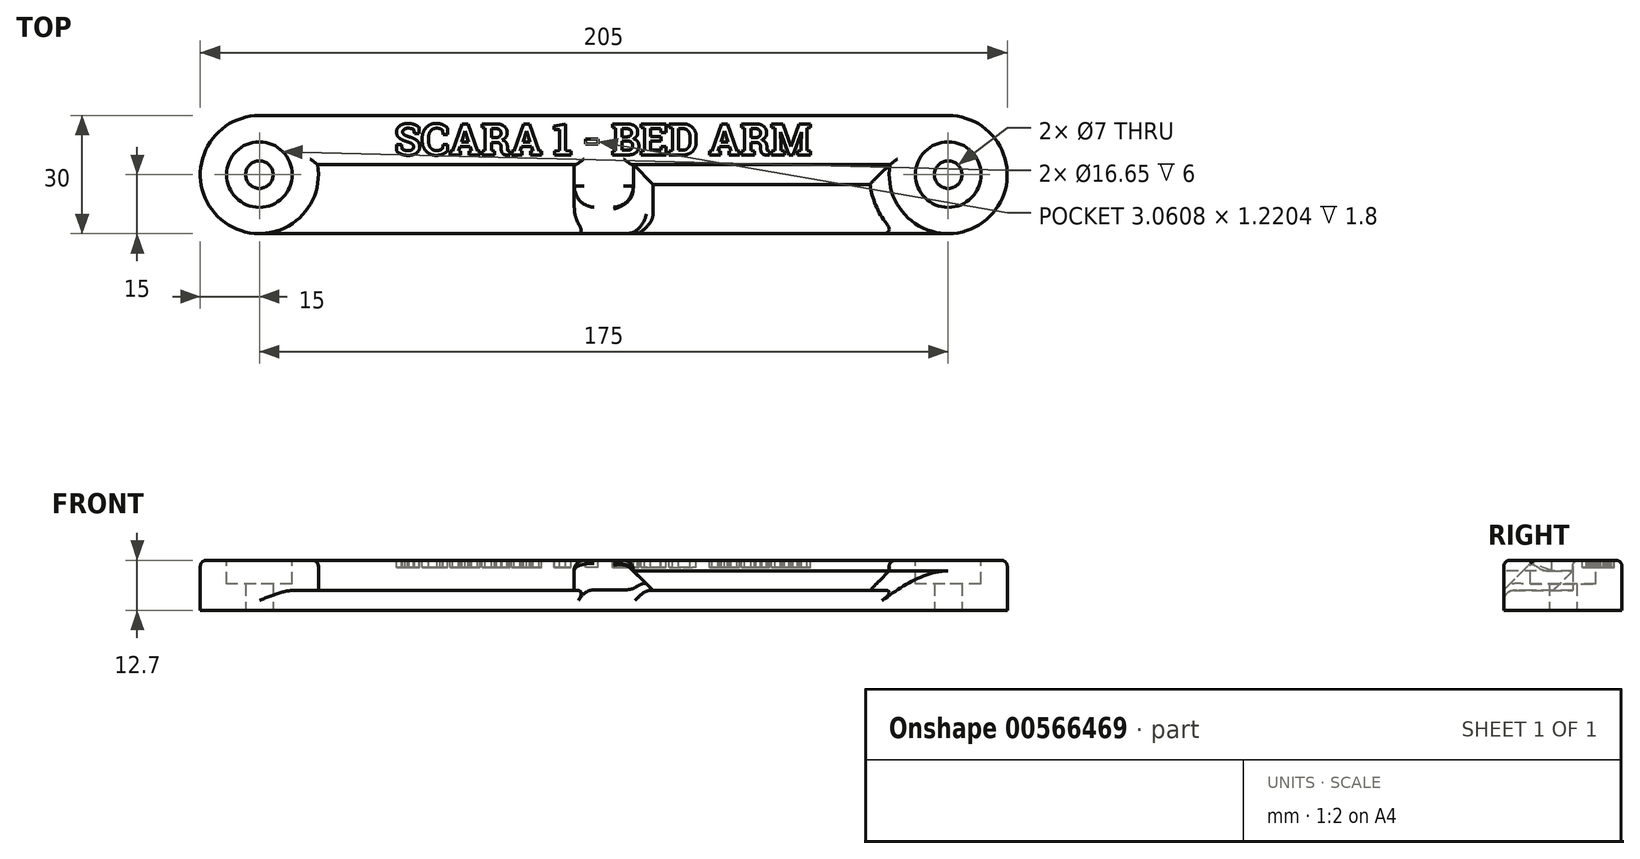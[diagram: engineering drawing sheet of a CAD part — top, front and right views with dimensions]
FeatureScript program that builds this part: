
annotation { "Feature Type Name" : "Feature", "Feature Type Description" : "" }
export const myFeature = defineFeature(function(context is Context, id is Id, definition is map)
    precondition{}
    {
        {
            var Q0;
            Q0=qCreatedBy(makeId("Top.planeOp"),FACE);
            var sketch = newSketch(context, id + "F0", { "sketchPlane" : qUnion([Q0])});
            skCircle(sketch, "E0", {"center": v(-87.5, 0) * mm, "radius": 8.62 * mm, "construction": true});
            skCircle(sketch, "E1.MirrorC", {"center": v(87.5, 0) * mm, "radius": 8.62 * mm, "construction": true});
            skArc(sketch, "E2", {"start": v(-87.5, 15) * mm, "mid": v(-102.5, 0) * mm, "end": v(-87.5, -15) * mm});
            skCircle(sketch, "E3", {"center": v(-87.5, 0) * mm, "radius": 3.5 * mm});
            skCircle(sketch, "E4.MirrorC", {"center": v(87.5, 0) * mm, "radius": 3.5 * mm});
            skArc(sketch, "E5.MirrorCS", {"start": v(87.5, 15) * mm, "mid": v(102.5, 0) * mm, "end": v(87.5, -15) * mm});
            skLineSegment(sketch, "E6", {"start": v(-87.5, -15) * mm, "end": v(87.5, -15) * mm});
            skLineSegment(sketch, "E7.MirrorCS", {"start": v(-87.5, 15) * mm, "end": v(87.5, 15) * mm});
            skSolve(sketch);
        }
        {
            var Q0;
            Q0=qSketchRegion(id+"F0",true);
            extrude(context, id + "F1", {"entities" : qUnion([Q0]), "depth" : 5 * mm, "offsetDistance" : 25 * mm});
        }
        {
            var Q0;
            Q0=makeQuery(id+"F1.opExtrude","CAP_FACE",FACE,{"disambiguationData":[OSD([sQuery(id+"F0.wireOp",EDGE,"E0"),sQuery(id+"F0.wireOp",EDGE,"E1.MirrorC"),sQuery(id+"F0.wireOp",EDGE,"E2"),sQuery(id+"F0.wireOp",EDGE,"E5.MirrorCS"),sQuery(id+"F0.wireOp",EDGE,"E6"),sQuery(id+"F0.wireOp",EDGE,"E7.MirrorCS")])],"isStart":false});
            var sketch = newSketch(context, id + "F2", { "sketchPlane" : qUnion([Q0])});
            skCircle(sketch, "E8", {"center": v(-87.5, 0) * mm, "radius": 3.5 * mm});
            skArc(sketch, "E9", {"start": v(-87.5, 15) * mm, "mid": v(-102.5, 0) * mm, "end": v(-87.5, -15) * mm});
            skCircle(sketch, "E10.MirrorC", {"center": v(87.5, 0) * mm, "radius": 3.5 * mm});
            skArc(sketch, "E11.MirrorCS", {"start": v(87.5, 15) * mm, "mid": v(102.5, 0) * mm, "end": v(87.5, -15) * mm});
            skArc(sketch, "E12", {"start": v(-72.7, 2.5) * mm, "mid": v(-76.04, -9.68) * mm, "end": v(-87.5, -15) * mm});
            skArc(sketch, "E13.MirrorCS", {"start": v(72.7, 2.5) * mm, "mid": v(76.04, -9.68) * mm, "end": v(87.5, -15) * mm});
            skLineSegment(sketch, "E14", {"start": v(-72.7, 2.5) * mm, "end": v(-7.5, 2.5) * mm});
            skLineSegment(sketch, "E15", {"start": v(-87.5, 15) * mm, "end": v(87.5, 15) * mm});
            skLineSegment(sketch, "E16", {"start": v(-7.5, 2.5) * mm, "end": v(-7.5, -15) * mm});
            skLineSegment(sketch, "E17", {"start": v(-7.5, -15) * mm, "end": v(0, -15) * mm});
            skLineSegment(sketch, "E18.MirrorCS", {"start": v(7.5, 2.5) * mm, "end": v(7.5, -15) * mm});
            skLineSegment(sketch, "E19.MirrorCS", {"start": v(7.5, -15) * mm, "end": v(0, -15) * mm});
            skLineSegment(sketch, "E20.trimOffspring", {"start": v(7.5, 2.5) * mm, "end": v(72.7, 2.5) * mm});
            skSolve(sketch);
        }
        {
            var Q0;
            Q0=qSketchRegion(id+"F2",true);
            extrude(context, id + "F3", {"entities" : qUnion([Q0]), "operationType" : NewBodyOperationType.ADD, "depth" : 7.7 * mm, "offsetDistance" : 25 * mm});
        }
        {
            var Q0;
            Q0=makeQuery(id+"F3.opExtrude","CAP_EDGE",EDGE,{"disambiguationData":[OSD([sQuery(id+"F2.wireOp",EDGE,"E14")])],"isStart":true});
            var Q1;
            Q1=makeQuery(id+"F3.opExtrude","CAP_EDGE",EDGE,{"disambiguationData":[OSD([sQuery(id+"F2.wireOp",EDGE,"E9"),sQuery(id+"F2.wireOp",EDGE,"E12")])],"isStart":true});
            var Q2;
            Q2=makeQuery(id+"F3.opExtrude","CAP_EDGE",EDGE,{"disambiguationData":[OSD([sQuery(id+"F2.wireOp",EDGE,"E11.MirrorCS"),sQuery(id+"F2.wireOp",EDGE,"E13.MirrorCS")])],"isStart":true});
            var Q3;
            Q3=makeQuery(id+"F3.opExtrude","CAP_EDGE",EDGE,{"disambiguationData":[OSD([sQuery(id+"F2.wireOp",EDGE,"E16")])],"isStart":true});
            var Q4;
            Q4=makeQuery(id+"F3.opExtrude","CAP_EDGE",EDGE,{"disambiguationData":[OSD([sQuery(id+"F2.wireOp",EDGE,"E18.MirrorCS")])],"isStart":true});
            var Q5;
            Q5=makeQuery(id+"F3.opExtrude","CAP_EDGE",EDGE,{"disambiguationData":[OSD([sQuery(id+"F2.wireOp",EDGE,"E20.trimOffspring")])],"isStart":true});
            chamfer(context, id + "F4", {"entities" : qUnion([Q0, Q1, Q2, Q3, Q4, Q5]), "width" : 5 * mm, "tangentPropagation" : true});
        }
        {
            var Q0;
            Q0=makeQuery(id+"F3.opExtrude","CAP_EDGE",EDGE,{"disambiguationData":[OSD([sQuery(id+"F2.wireOp",EDGE,"E17"),sQuery(id+"F2.wireOp",EDGE,"E19.MirrorCS")])],"isStart":false});
            chamfer(context, id + "F5", {"entities" : qUnion([Q0]), "width" : 7.5 * mm, "tangentPropagation" : true});
        }
        {
            var Q0;
            Q0=makeQuery(id+"F3.opExtrude","CAP_FACE",FACE,{"disambiguationData":[OSD([sQuery(id+"F2.wireOp",EDGE,"E8"),sQuery(id+"F2.wireOp",EDGE,"E9"),sQuery(id+"F2.wireOp",EDGE,"E10.MirrorC"),sQuery(id+"F2.wireOp",EDGE,"E11.MirrorCS"),sQuery(id+"F2.wireOp",EDGE,"E12"),sQuery(id+"F2.wireOp",EDGE,"E13.MirrorCS"),sQuery(id+"F2.wireOp",EDGE,"E14"),sQuery(id+"F2.wireOp",EDGE,"E15"),sQuery(id+"F2.wireOp",EDGE,"E16"),sQuery(id+"F2.wireOp",EDGE,"E17"),sQuery(id+"F2.wireOp",EDGE,"E18.MirrorCS"),sQuery(id+"F2.wireOp",EDGE,"E19.MirrorCS"),sQuery(id+"F2.wireOp",EDGE,"E20.trimOffspring")])],"isStart":false});
            var sketch = newSketch(context, id + "F6", { "sketchPlane" : qUnion([Q0])});
            skCircle(sketch, "E21", {"center": v(-87.5, 0) * mm, "radius": 8.32 * mm});
            skCircle(sketch, "E22.MirrorC", {"center": v(87.5, 0) * mm, "radius": 8.32 * mm});
            skSolve(sketch);
        }
        {
            var Q0;
            Q0=qSketchRegion(id+"F6",true);
            extrude(context, id + "F7", {"entities" : qUnion([Q0]), "operationType" : NewBodyOperationType.REMOVE, "oppositeDirection" : true, "depth" : 6 * mm, "offsetDistance" : 25 * mm});
        }
        {
            var Q0;
            Q0=makeQuery(id+"F3.opExtrude","CAP_FACE",FACE,{"disambiguationData":[OSD([sQuery(id+"F2.wireOp",EDGE,"E8"),sQuery(id+"F2.wireOp",EDGE,"E9"),sQuery(id+"F2.wireOp",EDGE,"E10.MirrorC"),sQuery(id+"F2.wireOp",EDGE,"E11.MirrorCS"),sQuery(id+"F2.wireOp",EDGE,"E12"),sQuery(id+"F2.wireOp",EDGE,"E13.MirrorCS"),sQuery(id+"F2.wireOp",EDGE,"E14"),sQuery(id+"F2.wireOp",EDGE,"E15"),sQuery(id+"F2.wireOp",EDGE,"E16"),sQuery(id+"F2.wireOp",EDGE,"E17"),sQuery(id+"F2.wireOp",EDGE,"E18.MirrorCS"),sQuery(id+"F2.wireOp",EDGE,"E19.MirrorCS"),sQuery(id+"F2.wireOp",EDGE,"E20.trimOffspring")])],"isStart":false});
            var sketch = newSketch(context, id + "F8", { "sketchPlane" : qUnion([Q0])});
            skText(sketch, "E23", { "text": "SCARA 1 - BED ARM", "fontName": "RobotoSlab-Bold.ttf"});
            const initialGuessF8  = {"E23": [-0.05318, 0.005, 1, 0, 0.008]};
            skSetInitialGuess(sketch, initialGuessF8);
            skSolve(sketch);
        }
        {
            var Q0;
            Q0=qSketchRegion(id+"F8",true);
            extrude(context, id + "F9", {"entities" : qUnion([Q0]), "operationType" : NewBodyOperationType.REMOVE, "oppositeDirection" : true, "depth" : 1.8 * mm});
        }
        {
            var Q0;
            Q0=makeQuery(id+"F5.opChamfer","BLEND_EDGE",EDGE,{"blendedFrom":[makeQuery(id+"F3.opExtrude","CAP_EDGE",EDGE,{"disambiguationData":[OSD([sQuery(id+"F2.wireOp",EDGE,"E17"),sQuery(id+"F2.wireOp",EDGE,"E19.MirrorCS")])],"isStart":false}),makeQuery(id+"F3.opExtrude","SWEPT_FACE",FACE,{"disambiguationData":[OSD([sQuery(id+"F2.wireOp",EDGE,"E16")])]})],"blendedInto":[makeQuery(id+"F3.opExtrude","SWEPT_FACE",FACE,{"disambiguationData":[OSD([sQuery(id+"F2.wireOp",EDGE,"E16")])]})]});
            var Q1;
            Q1=makeQuery(id+"F5.opChamfer","BLEND_EDGE",EDGE,{"blendedFrom":[makeQuery(id+"F3.opExtrude","CAP_EDGE",EDGE,{"disambiguationData":[OSD([sQuery(id+"F2.wireOp",EDGE,"E17"),sQuery(id+"F2.wireOp",EDGE,"E19.MirrorCS")])],"isStart":false}),makeQuery(id+"F3.opExtrude","SWEPT_FACE",FACE,{"disambiguationData":[OSD([sQuery(id+"F2.wireOp",EDGE,"E18.MirrorCS")])]})],"blendedInto":[makeQuery(id+"F3.opExtrude","SWEPT_FACE",FACE,{"disambiguationData":[OSD([sQuery(id+"F2.wireOp",EDGE,"E18.MirrorCS")])]})]});
            var Q2;
            Q2=makeQuery(id+"F5.opChamfer","BLEND_EDGE",EDGE,{"blendedFrom":[makeQuery(id+"F3.opExtrude","CAP_EDGE",EDGE,{"disambiguationData":[OSD([sQuery(id+"F2.wireOp",EDGE,"E17"),sQuery(id+"F2.wireOp",EDGE,"E19.MirrorCS")])],"isStart":false}),makeQuery(id+"F4.opChamfer","BLEND_FACE",FACE,{"disambiguationData":[OSD([sQuery(id+"F2.wireOp",EDGE,"E18.MirrorCS")])]})],"blendedInto":[makeQuery(id+"F4.opChamfer","BLEND_FACE",FACE,{"disambiguationData":[OSD([sQuery(id+"F2.wireOp",EDGE,"E18.MirrorCS")])]})]});
            var Q3;
            Q3=makeQuery(id+"F5.opChamfer","BLEND_EDGE",EDGE,{"blendedFrom":[makeQuery(id+"F3.opExtrude","CAP_EDGE",EDGE,{"disambiguationData":[OSD([sQuery(id+"F2.wireOp",EDGE,"E17"),sQuery(id+"F2.wireOp",EDGE,"E19.MirrorCS")])],"isStart":false}),makeQuery(id+"F4.opChamfer","BLEND_FACE",FACE,{"disambiguationData":[OSD([sQuery(id+"F2.wireOp",EDGE,"E16")])]})],"blendedInto":[makeQuery(id+"F4.opChamfer","BLEND_FACE",FACE,{"disambiguationData":[OSD([sQuery(id+"F2.wireOp",EDGE,"E16")])]})]});
            var Q4;
            Q4=makeQuery(id+"F4.opChamfer","BLEND_EDGE",EDGE,{"blendedFrom":[makeQuery(id+"F3.opExtrude","CAP_EDGE",EDGE,{"disambiguationData":[OSD([sQuery(id+"F2.wireOp",EDGE,"E18.MirrorCS")])],"isStart":true}),makeQuery(id+"F3.boolean.opBoolean","MERGE",FACE,{"derivedFrom":[makeQuery(id+"F1.opExtrude","SWEPT_FACE",FACE,{"disambiguationData":[OSD([sQuery(id+"F0.wireOp",EDGE,"E6")])]}),makeQuery(id+"F3.opExtrude","SWEPT_FACE",FACE,{"disambiguationData":[OSD([sQuery(id+"F2.wireOp",EDGE,"E17"),sQuery(id+"F2.wireOp",EDGE,"E19.MirrorCS")])]})]})],"blendedInto":[makeQuery(id+"F3.boolean.opBoolean","MERGE",FACE,{"derivedFrom":[makeQuery(id+"F1.opExtrude","SWEPT_FACE",FACE,{"disambiguationData":[OSD([sQuery(id+"F0.wireOp",EDGE,"E6")])]}),makeQuery(id+"F3.opExtrude","SWEPT_FACE",FACE,{"disambiguationData":[OSD([sQuery(id+"F2.wireOp",EDGE,"E17"),sQuery(id+"F2.wireOp",EDGE,"E19.MirrorCS")])]})]})]});
            var Q5;
            Q5=makeQuery(id+"F4.opChamfer","BLEND_EDGE",EDGE,{"blendedFrom":[makeQuery(id+"F3.opExtrude","CAP_EDGE",EDGE,{"disambiguationData":[OSD([sQuery(id+"F2.wireOp",EDGE,"E16")])],"isStart":true}),makeQuery(id+"F3.boolean.opBoolean","MERGE",FACE,{"derivedFrom":[makeQuery(id+"F1.opExtrude","SWEPT_FACE",FACE,{"disambiguationData":[OSD([sQuery(id+"F0.wireOp",EDGE,"E6")])]}),makeQuery(id+"F3.opExtrude","SWEPT_FACE",FACE,{"disambiguationData":[OSD([sQuery(id+"F2.wireOp",EDGE,"E17"),sQuery(id+"F2.wireOp",EDGE,"E19.MirrorCS")])]})]})],"blendedInto":[makeQuery(id+"F3.boolean.opBoolean","MERGE",FACE,{"derivedFrom":[makeQuery(id+"F1.opExtrude","SWEPT_FACE",FACE,{"disambiguationData":[OSD([sQuery(id+"F0.wireOp",EDGE,"E6")])]}),makeQuery(id+"F3.opExtrude","SWEPT_FACE",FACE,{"disambiguationData":[OSD([sQuery(id+"F2.wireOp",EDGE,"E17"),sQuery(id+"F2.wireOp",EDGE,"E19.MirrorCS")])]})]})]});
            fillet(context, id + "F10", {"entities" : qUnion([Q0, Q1, Q2, Q3, Q4, Q5]), "radius" : 5 * mm, "tangentPropagation" : true, "allowEdgeOverflow" : false});
        }
        {
            var Q0;
            Q0=makeQuery(id+"F3.opExtrude","CAP_EDGE",EDGE,{"disambiguationData":[OSD([sQuery(id+"F2.wireOp",EDGE,"E11.MirrorCS"),sQuery(id+"F2.wireOp",EDGE,"E13.MirrorCS")])],"isStart":false});
            var Q1;
            Q1=makeQuery(id+"F3.opExtrude","CAP_EDGE",EDGE,{"disambiguationData":[OSD([sQuery(id+"F2.wireOp",EDGE,"E20.trimOffspring")])],"isStart":false});
            var Q2;
            Q2=makeQuery(id+"F3.opExtrude","CAP_EDGE",EDGE,{"disambiguationData":[OSD([sQuery(id+"F2.wireOp",EDGE,"E14")])],"isStart":false});
            fillet(context, id + "F11", {"entities" : qUnion([Q0, Q1, Q2]), "radius" : 1.5 * mm, "tangentPropagation" : true, "allowEdgeOverflow" : false});
        }
        {
            var Q0;
            {var subQ0=sQuery(id+"F0.wireOp",EDGE,"E6");var subQ1=sQuery(id+"F0.wireOp",EDGE,"E2");Q0=makeQuery(id+"F3.boolean.opBoolean","SPLIT",EDGE,{"disambiguationData":[TD([makeQuery(id+"F1.opExtrude","SWEPT_FACE",FACE,{"disambiguationData":[OSD([subQ1])]})])],"derivedFrom":makeQuery(id+"F1.opExtrude","CAP_EDGE",EDGE,{"disambiguationData":[OSD([subQ0])],"isStart":false})});}
            var Q1;
            {var subQ0=sQuery(id+"F0.wireOp",EDGE,"E6");var subQ1=sQuery(id+"F0.wireOp",EDGE,"E5.MirrorCS");Q1=makeQuery(id+"F3.boolean.opBoolean","SPLIT",EDGE,{"disambiguationData":[TD([makeQuery(id+"F1.opExtrude","SWEPT_FACE",FACE,{"disambiguationData":[OSD([subQ1])]})])],"derivedFrom":makeQuery(id+"F1.opExtrude","CAP_EDGE",EDGE,{"disambiguationData":[OSD([subQ0])],"isStart":false})});}
            fillet(context, id + "F12", {"entities" : qUnion([Q0, Q1]), "radius" : 2.5 * mm, "tangentPropagation" : true, "allowEdgeOverflow" : false});
        }
        {
            var Q0;
            Q0=makeQuery(id+"F3.opExtrude","CAP_EDGE",EDGE,{"disambiguationData":[OSD([sQuery(id+"F2.wireOp",EDGE,"E16")])],"isStart":false});
            var Q1;
            Q1=makeQuery(id+"F3.opExtrude","CAP_EDGE",EDGE,{"disambiguationData":[OSD([sQuery(id+"F2.wireOp",EDGE,"E18.MirrorCS")])],"isStart":false});
            fillet(context, id + "F13", {"entities" : qUnion([Q0, Q1]), "radius" : 2.5 * mm, "tangentPropagation" : true, "allowEdgeOverflow" : false});
        }
    });
